# Revit family: Domotics-DomesticRanges-GEWISS-CHORUS_DATA-SOCKET-OUTLET_COVER_2M
name_source: partatom
category: Apparecchi elettrici
revit_build: Autodesk Revit 2016 (Build: 20161004_0715(x64)
units: mm (PartAtom-declared; Revit-internal decimal feet)

## family parameters
Condiviso = Sì
Host = Superficie
Mantenere orientamento annotazione = Sì
Numero OmniClass = 23.80.50.14
Punto di calcolo locali = Sì
Quota connettore circolare = Usa diametro
Taglio con vuoti quando caricato = Sì
Tipo di parte = Normale
Titolo OmniClass = Plug Connectors

## types (3) — shared parameters
Catalogue = DOMOTICS
Catalogue Range = CHORUS - DOMESTIC RANGE
Category = Adapter
Compatibility: = AMP / Keystone Jack
Description. = Adapter
IDF = c47c3d4f-2792-405f-abb5-cbfa4f4237f7
IDT = 98683686-5171-427a-bec0-d475def51726
Immagine tipo = GW14433.jpg
Larghezza presa = 46 mm  [stored 0.150919 ft]
No. Chorus modules: = 2
Produttore = GEWISS S.p.A.
Prospetto di default = 1219 mm
SEO = Container
Simbolo = SIMBOLO PRESE TELEFONO : PRESA TEL
Technical sheet = https://www.gewiss.com
Tipo = SYSTEM PRESE RJ45_BASE : RJ45 Titanio
URL = https://www.gewiss.com
Version file RFA = 19.0

## per-type parameters (varying)
| type | Colour | Descrizione | EAN code | Electrocod | Modello |
| GW14433 - UNWIRED ENCLOS.RJ45 2M.CONNEC TITANIUM | Titanium | UNWIRED ENCLOS.RJ45 2M.CONNEC TITANIUM | 8011564823815 | 3722 | GW14433 |
| GW12433 - UNWIRED ENCLOS.RJ45 2M.CONNEC BLACK | Black | UNWIRED ENCLOS.RJ45 2M.CONNEC BLACK | 8011564823808 | 3722 | GW12433 |
| GW10433 - UNWIRED ENCLOS.RJ45 CONNEC 2M. WHITE | White | UNWIRED ENCLOS.RJ45 CONNEC 2M. WHITE | 8011564823792 | 0131 | GW10433 |

note: [stored X ft] marks values corroborated as IEEE doubles in the binary element streams (Revit-internal decimal feet)

## geometry (parser evidence)
native form markers: Sweep x2
no freeform markers — native parametric forms only
